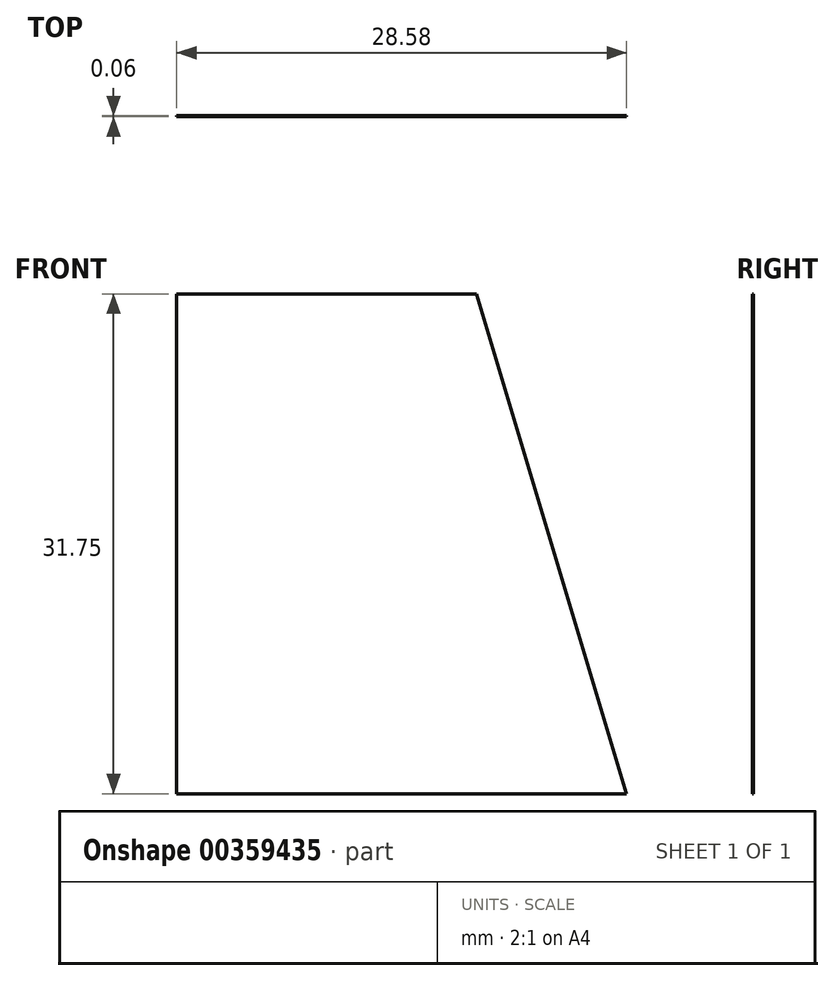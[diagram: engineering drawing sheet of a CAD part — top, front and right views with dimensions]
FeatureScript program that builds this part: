
annotation { "Feature Type Name" : "Feature", "Feature Type Description" : "" }
export const myFeature = defineFeature(function(context is Context, id is Id, definition is map)
    precondition{}
    {
        {
            var Q0;
            Q0=qCreatedBy(makeId("Front.planeOp"),FACE);
            var sketch = newSketch(context, id + "F0", { "sketchPlane" : qUnion([Q0])});
            skLineSegment(sketch, "E0", {"start": v(0, 0) * mm, "end": v(0, 31.75) * mm});
            skLineSegment(sketch, "E1", {"start": v(0, 31.75) * mm, "end": v(57.15, 31.75) * mm});
            skLineSegment(sketch, "E2", {"start": v(57.15, 31.75) * mm, "end": v(57.15, 0) * mm});
            skLineSegment(sketch, "E3", {"start": v(57.15, 0) * mm, "end": v(0, 0) * mm});
            skSolve(sketch);
        }
        {
            var Q0;
            Q0=makeQuery(id+"F0.imprint","IMPRINT",FACE,{"disambiguationData":[TD([[makeQuery(id+"F0.imprint","IMPRINT",EDGE,{"derivedFrom":sQuery(id+"F0.wireOp",EDGE,"E0")}),-1.0]])]});
            extrude(context, id + "F1", {"entities" : qUnion([Q0]), "depth" : 6 / 101.6 * mm});
        }
        {
            var Q0;
            Q0=makeQuery(id+"F1.opExtrude","CAP_FACE",FACE,{"disambiguationData":[OSD([sQuery(id+"F0.wireOp",EDGE,"E0"),sQuery(id+"F0.wireOp",EDGE,"E1"),sQuery(id+"F0.wireOp",EDGE,"E2"),sQuery(id+"F0.wireOp",EDGE,"E3")])],"isStart":false});
            var sketch = newSketch(context, id + "F2", { "sketchPlane" : qUnion([Q0])});
            skLineSegment(sketch, "E4", {"start": v(57.15, 0) * mm, "end": v(44.45, 31.75) * mm});
            skLineSegment(sketch, "E5", {"start": v(44.45, 31.75) * mm, "end": v(57.15, 31.75) * mm});
            skLineSegment(sketch, "E6", {"start": v(57.15, 31.75) * mm, "end": v(57.15, 0) * mm});
            skSolve(sketch);
        }
        {
            var Q0;
            Q0=makeQuery(id+"F2.imprint","IMPRINT",FACE,{"disambiguationData":[TD([[makeQuery(id+"F2.imprint","IMPRINT",EDGE,{"derivedFrom":sQuery(id+"F2.wireOp",EDGE,"E4")}),-1.0]])]});
            extrude(context, id + "F3", {"entities" : qUnion([Q0]), "operationType" : NewBodyOperationType.REMOVE, "oppositeDirection" : true, "depth" : 6 / 101.6 * mm});
        }
        {
            var Q0;
            Q0=makeQuery(id+"F1.opExtrude","CAP_FACE",FACE,{"disambiguationData":[OSD([sQuery(id+"F0.wireOp",EDGE,"E0"),sQuery(id+"F0.wireOp",EDGE,"E1"),sQuery(id+"F0.wireOp",EDGE,"E2"),sQuery(id+"F0.wireOp",EDGE,"E3")])],"isStart":true});
            var sketch = newSketch(context, id + "F4", { "sketchPlane" : qUnion([Q0])});
            skLineSegment(sketch, "E7", {"start": v(-57.15, 0) * mm, "end": v(-44.45, 31.75) * mm});
            skLineSegment(sketch, "E8", {"start": v(-44.45, 31.75) * mm, "end": v(-19.05, 31.75) * mm});
            skLineSegment(sketch, "E9", {"start": v(-19.05, 31.75) * mm, "end": v(-28.57, 0) * mm});
            skLineSegment(sketch, "E10", {"start": v(-28.58, 0) * mm, "end": v(-57.15, 0) * mm});
            skSolve(sketch);
        }
        {
            var Q0;
            Q0=makeQuery(id+"F4.imprint","IMPRINT",FACE,{"disambiguationData":[TD([[makeQuery(id+"F4.imprint","IMPRINT",EDGE,{"derivedFrom":sQuery(id+"F4.wireOp",EDGE,"E7")}),-1.0]])]});
            extrude(context, id + "F5", {"entities" : qUnion([Q0]), "operationType" : NewBodyOperationType.REMOVE, "oppositeDirection" : true, "depth" : 12.7 * mm});
        }
        {
            var Q0;
            Q0=makeQuery(id+"F1.opExtrude","CAP_FACE",FACE,{"disambiguationData":[OSD([sQuery(id+"F0.wireOp",EDGE,"E0"),sQuery(id+"F0.wireOp",EDGE,"E1"),sQuery(id+"F0.wireOp",EDGE,"E2"),sQuery(id+"F0.wireOp",EDGE,"E3")])],"isStart":false});
            var sketch = newSketch(context, id + "F6", { "sketchPlane" : qUnion([Q0])});
            skLineSegment(sketch, "E11", {"start": v(57.15, 0) * mm, "end": v(44.45, 31.75) * mm});
            skLineSegment(sketch, "E12", {"start": v(44.45, 31.75) * mm, "end": v(19.05, 31.75) * mm});
            skLineSegment(sketch, "E13", {"start": v(19.05, 31.75) * mm, "end": v(31.75, 0) * mm});
            skLineSegment(sketch, "E14", {"start": v(31.75, 0) * mm, "end": v(57.15, 0) * mm});
            skSolve(sketch);
        }
        {
            var Q0;
            Q0=makeQuery(id+"F6.imprint","IMPRINT",FACE,{"disambiguationData":[TD([[makeQuery(id+"F6.imprint","IMPRINT",EDGE,{"derivedFrom":sQuery(id+"F6.wireOp",EDGE,"E11")}),1.0]])]});
            extrude(context, id + "F7", {"entities" : qUnion([Q0]), "operationType" : NewBodyOperationType.REMOVE, "oppositeDirection" : true, "depth" : 12.7 * mm});
        }
    });
